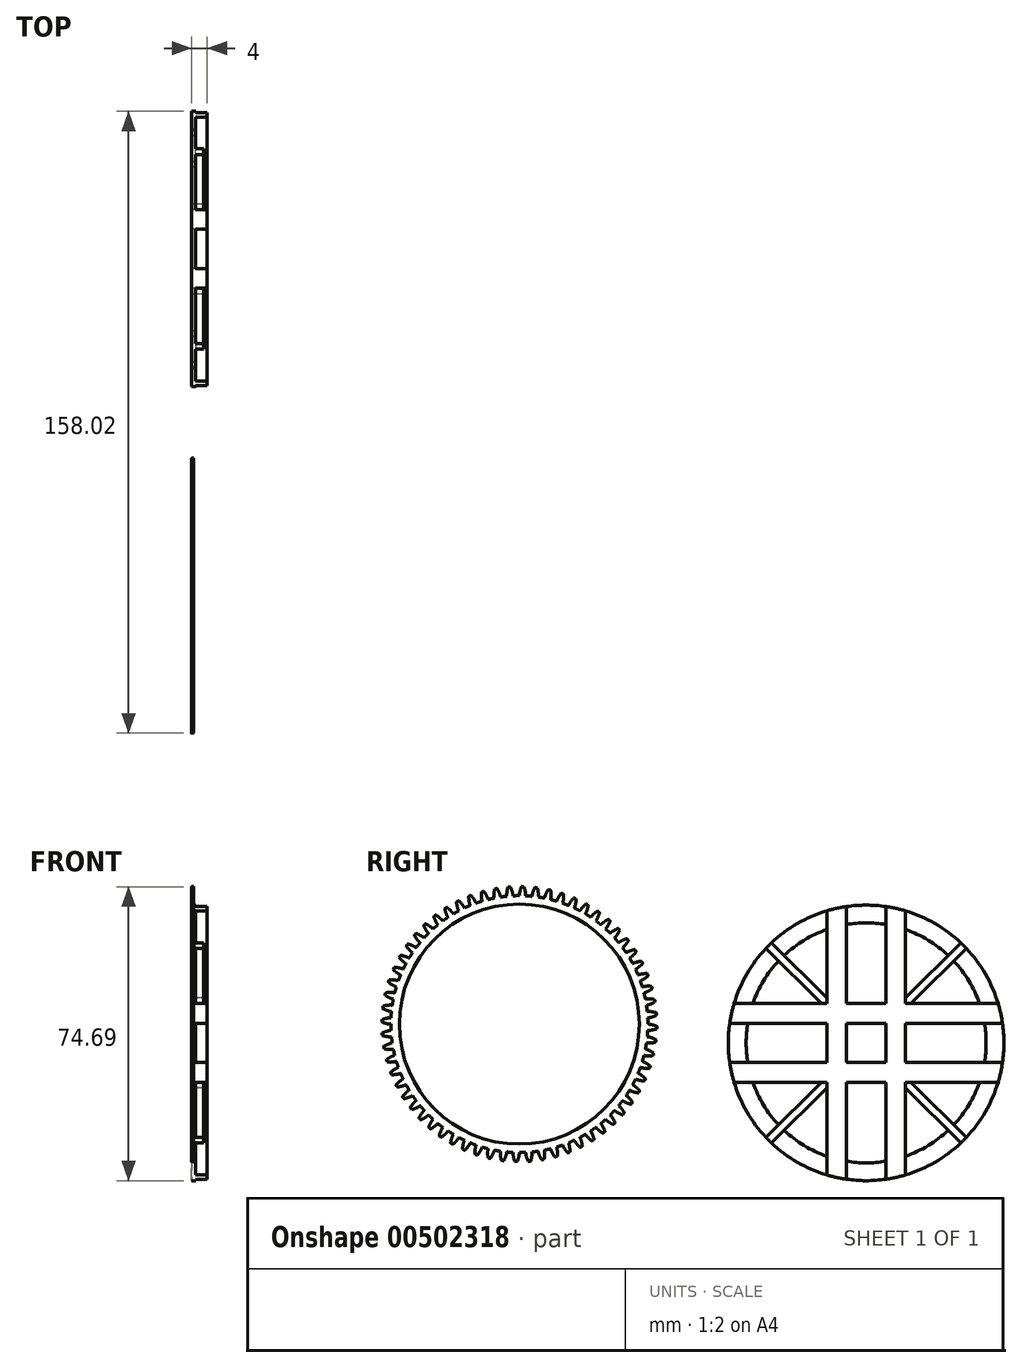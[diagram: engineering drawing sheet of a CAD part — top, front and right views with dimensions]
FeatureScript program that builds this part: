
annotation { "Feature Type Name" : "Feature", "Feature Type Description" : "" }
export const myFeature = defineFeature(function(context is Context, id is Id, definition is map)
    precondition{}
    {
        {
            assignVariable(context, id + "F0", {"name" : "NumberTeeth", "anyValue" : 64});
        }
        {
            assignVariable(context, id + "F1", {"name" : "GearThickness", "anyValue" : .5});
        }
        {
            var Q0;
            Q0=qCreatedBy(makeId("Right.planeOp"),FACE);
            var sketch = newSketch(context, id + "F2", { "sketchPlane" : qUnion([Q0])});
            skCircle(sketch, "E0", {"center": v(0, 0) * mm, "radius": 32.64 * mm});
            skCircle(sketch, "E1", {"center": v(0, 0) * mm, "radius": 32.79 * mm, "construction": true});
            skCircle(sketch, "E2", {"center": v(0, 0) * mm, "radius": 33.87 * mm, "construction": true});
            skCircle(sketch, "E3", {"center": v(0, 0) * mm, "radius": 34.93 * mm});
            skLineSegment(sketch, "E4", {"start": v(0, 0) * mm, "end": v(-32.79, 0) * mm, "construction": true});
            skLineSegment(sketch, "E5.1.0", {"start": v(0, 0) * mm, "end": v(-32.75, 1.64) * mm, "construction": true});
            skLineSegment(sketch, "E5.2.0", {"start": v(0, 0) * mm, "end": v(-32.62, 3.27) * mm, "construction": true});
            skLineSegment(sketch, "E5.3.0", {"start": v(0, 0) * mm, "end": v(-32.42, 4.9) * mm, "construction": true});
            skLineSegment(sketch, "E5.4.0", {"start": v(0, 0) * mm, "end": v(-32.13, 6.51) * mm, "construction": true});
            skLineSegment(sketch, "E5.5.0", {"start": v(0, 0) * mm, "end": v(-31.77, 8.11) * mm, "construction": true});
            skLineSegment(sketch, "E5.6.0", {"start": v(0, 0) * mm, "end": v(-31.32, 9.69) * mm, "construction": true});
            skLineSegment(sketch, "E5.7.0", {"start": v(0, 0) * mm, "end": v(-30.8, 11.24) * mm, "construction": true});
            skLineSegment(sketch, "E5.8.0", {"start": v(0, 0) * mm, "end": v(-30.2, 12.77) * mm, "construction": true});
            skLineSegment(sketch, "E5.9.0", {"start": v(0, 0) * mm, "end": v(-29.52, 14.26) * mm, "construction": true});
            skLineSegment(sketch, "E5.10.0", {"start": v(0, 0) * mm, "end": v(-28.77, 15.72) * mm, "construction": true});
            skLineSegment(sketch, "E5.11.0", {"start": v(0, 0) * mm, "end": v(-27.95, 17.14) * mm, "construction": true});
            skLineSegment(sketch, "E5.12.0", {"start": v(0, 0) * mm, "end": v(-27.06, 18.51) * mm, "construction": true});
            skLineSegment(sketch, "E5.13.0", {"start": v(0, 0) * mm, "end": v(-26.1, 19.84) * mm, "construction": true});
            skLineSegment(sketch, "E5.14.0", {"start": v(0, 0) * mm, "end": v(-25.08, 21.12) * mm, "construction": true});
            skLineSegment(sketch, "E5.anchor2", {"start": v(0, 0) * mm, "end": v(-25.08, 21.12) * mm, "construction": true});
            skLineSegment(sketch, "E6", {"start": v(-32.75, 1.64) * mm, "end": v(-32.83, 0) * mm, "construction": true});
            skLineSegment(sketch, "E7", {"start": v(-32.62, 3.27) * mm, "end": v(-32.95, 0.01) * mm, "construction": true});
            skLineSegment(sketch, "E8", {"start": v(-32.42, 4.9) * mm, "end": v(-33.15, 0.04) * mm, "construction": true});
            skLineSegment(sketch, "E9", {"start": v(-31.77, 8.11) * mm, "end": v(-33.8, 0.17) * mm, "construction": true});
            skLineSegment(sketch, "E10", {"start": v(-31.32, 9.69) * mm, "end": v(-34.23, 0.3) * mm, "construction": true});
            skLineSegment(sketch, "E11", {"start": v(-30.8, 11.24) * mm, "end": v(-34.74, 0.46) * mm, "construction": true});
            skLineSegment(sketch, "E12", {"start": v(-30.2, 12.77) * mm, "end": v(-35.3, 0.69) * mm, "construction": true});
            skLineSegment(sketch, "E13", {"start": v(-29.52, 14.26) * mm, "end": v(-35.94, 0.98) * mm, "construction": true});
            skLineSegment(sketch, "E14", {"start": v(-28.77, 15.72) * mm, "end": v(-36.63, 1.33) * mm, "construction": true});
            skLineSegment(sketch, "E15", {"start": v(-27.95, 17.14) * mm, "end": v(-37.38, 1.76) * mm, "construction": true});
            skLineSegment(sketch, "E16", {"start": v(-32.13, 6.51) * mm, "end": v(-33.44, 0.09) * mm, "construction": true});
            skLineSegment(sketch, "E17", {"start": v(-27.06, 18.51) * mm, "end": v(-38.17, 2.28) * mm, "construction": true});
            skLineSegment(sketch, "E18", {"start": v(-26.1, 19.84) * mm, "end": v(-39, 2.88) * mm, "construction": true});
            skLineSegment(sketch, "E19", {"start": v(-25.08, 21.12) * mm, "end": v(-39.86, 3.57) * mm, "construction": true});
            skLineSegment(sketch, "E20", {"start": v(0, 0) * mm, "end": v(-32.78, 0.8) * mm, "construction": true});
            skLineSegment(sketch, "E21", {"start": v(-32.64, 0) * mm, "end": v(-32.79, 0) * mm});
            skLineSegment(sketch, "E22.MirrorCS", {"start": v(-32.6, 1.6) * mm, "end": v(-32.75, 1.6) * mm});
            skFitSpline(sketch, "E23", {"points": [v(-32.79, 0) * mm, v(-32.83, 0) * mm, v(-32.95, 0.01) * mm, v(-33.15, 0.04) * mm, v(-33.44, 0.09) * mm, v(-33.8, 0.17) * mm, v(-34.23, 0.3) * mm, v(-34.74, 0.46) * mm, v(-35.3, 0.69) * mm, v(-35.94, 0.98) * mm, v(-36.63, 1.33) * mm, v(-37.38, 1.76) * mm, v(-38.17, 2.28) * mm, v(-39, 2.88) * mm, v(-39.86, 3.57) * mm], "startDerivative": vector(-0.7, 0) * mm, "endDerivative": vector(-1.66, 1.4) * mm});
            skLineSegment(sketch, "E24", {"start": v(-26.9, -7.36) * mm, "end": v(-39.86, 3.57) * mm, "construction": true});
            skFitSpline(sketch, "E25.MirrorCS", {"points": [v(-32.75, 1.6) * mm, v(-32.79, 1.6) * mm, v(-32.91, 1.6) * mm, v(-33.12, 1.6) * mm, v(-33.4, 1.55) * mm, v(-33.76, 1.49) * mm, v(-34.2, 1.39) * mm, v(-34.72, 1.24) * mm, v(-35.3, 1.04) * mm, v(-35.95, 0.79) * mm, v(-36.66, 0.47) * mm, v(-37.42, 0.07) * mm, v(-38.23, -0.4) * mm, v(-39.1, -0.96) * mm, v(-40, -1.6) * mm], "startDerivative": vector(-0.7, 0.03) * mm, "endDerivative": vector(-1.73, -1.32) * mm});
            skCircle(sketch, "E26", {"center": v(0, 0) * mm, "radius": 30.48 * mm});
            skSolve(sketch);
        }
        {
            var Q0;
            {var subQ0=sQuery(id+"F2.wireOp",EDGE,"E0");var subQ27=makeQuery(id+"F2.imprint","INTERSECT",VERTEX,{"derivedFrom":[subQ0,sQuery(id+"F2.wireOp",EDGE,"10ea1024-8cf5-41f5-a75f-a634b86921f3.10.0")]});Q0=makeQuery(id+"F2.imprint","IMPRINT",FACE,{"disambiguationData":[TD([[makeQuery(id+"F2.imprint","IMPRINT",EDGE,{"disambiguationData":[TD([[subQ27,-1.0]])],"derivedFrom":subQ0}),1.0]])]});}
            var Q1;
            {var subQ0=sQuery(id+"F2.wireOp",EDGE,"10ea1024-8cf5-41f5-a75f-a634b86921f3.1.0");Q1=makeQuery(id+"F2.imprint","IMPRINT",FACE,{"disambiguationData":[TD([[makeQuery(id+"F2.imprint","IMPRINT",EDGE,{"derivedFrom":subQ0}),-1.0]])]});}
            var Q2;
            {var subQ7=sQuery(id+"F2.wireOp",EDGE,"10ea1024-8cf5-41f5-a75f-a634b86921f3.2.0");Q2=makeQuery(id+"F2.imprint","IMPRINT",FACE,{"disambiguationData":[TD([[makeQuery(id+"F2.imprint","IMPRINT",EDGE,{"derivedFrom":subQ7}),-1.0]])]});}
            var Q3;
            {var subQ8=sQuery(id+"F2.wireOp",EDGE,"10ea1024-8cf5-41f5-a75f-a634b86921f3.3.0");Q3=makeQuery(id+"F2.imprint","IMPRINT",FACE,{"disambiguationData":[TD([[makeQuery(id+"F2.imprint","IMPRINT",EDGE,{"derivedFrom":subQ8}),-1.0]])]});}
            var Q4;
            {var subQ2=sQuery(id+"F2.wireOp",EDGE,"10ea1024-8cf5-41f5-a75f-a634b86921f3.4.0");Q4=makeQuery(id+"F2.imprint","IMPRINT",FACE,{"disambiguationData":[TD([[makeQuery(id+"F2.imprint","IMPRINT",EDGE,{"derivedFrom":subQ2}),-1.0]])]});}
            var Q5;
            {var subQ8=sQuery(id+"F2.wireOp",EDGE,"10ea1024-8cf5-41f5-a75f-a634b86921f3.5.0");Q5=makeQuery(id+"F2.imprint","IMPRINT",FACE,{"disambiguationData":[TD([[makeQuery(id+"F2.imprint","IMPRINT",EDGE,{"derivedFrom":subQ8}),-1.0]])]});}
            var Q6;
            {var subQ3=sQuery(id+"F2.wireOp",EDGE,"10ea1024-8cf5-41f5-a75f-a634b86921f3.6.0");Q6=makeQuery(id+"F2.imprint","IMPRINT",FACE,{"disambiguationData":[TD([[makeQuery(id+"F2.imprint","IMPRINT",EDGE,{"derivedFrom":subQ3}),-1.0]])]});}
            var Q7;
            {var subQ0=sQuery(id+"F2.wireOp",EDGE,"10ea1024-8cf5-41f5-a75f-a634b86921f3.7.0");Q7=makeQuery(id+"F2.imprint","IMPRINT",FACE,{"disambiguationData":[TD([[makeQuery(id+"F2.imprint","IMPRINT",EDGE,{"derivedFrom":subQ0}),-1.0]])]});}
            var Q8;
            {var subQ5=sQuery(id+"F2.wireOp",EDGE,"10ea1024-8cf5-41f5-a75f-a634b86921f3.8.0");Q8=makeQuery(id+"F2.imprint","IMPRINT",FACE,{"disambiguationData":[TD([[makeQuery(id+"F2.imprint","IMPRINT",EDGE,{"derivedFrom":subQ5}),-1.0]])]});}
            var Q9;
            {var subQ1=sQuery(id+"F2.wireOp",EDGE,"10ea1024-8cf5-41f5-a75f-a634b86921f3.9.0");Q9=makeQuery(id+"F2.imprint","IMPRINT",FACE,{"disambiguationData":[TD([[makeQuery(id+"F2.imprint","IMPRINT",EDGE,{"derivedFrom":subQ1}),-1.0]])]});}
            var Q10;
            {var subQ5=sQuery(id+"F2.wireOp",EDGE,"10ea1024-8cf5-41f5-a75f-a634b86921f3.10.0");Q10=makeQuery(id+"F2.imprint","IMPRINT",FACE,{"disambiguationData":[TD([[makeQuery(id+"F2.imprint","IMPRINT",EDGE,{"derivedFrom":subQ5}),-1.0]])]});}
            var Q11;
            {var subQ8=sQuery(id+"F2.wireOp",EDGE,"10ea1024-8cf5-41f5-a75f-a634b86921f3.11.0");Q11=makeQuery(id+"F2.imprint","IMPRINT",FACE,{"disambiguationData":[TD([[makeQuery(id+"F2.imprint","IMPRINT",EDGE,{"derivedFrom":subQ8}),-1.0]])]});}
            var Q12;
            {var subQ2=sQuery(id+"F2.wireOp",EDGE,"10ea1024-8cf5-41f5-a75f-a634b86921f3.12.0");Q12=makeQuery(id+"F2.imprint","IMPRINT",FACE,{"disambiguationData":[TD([[makeQuery(id+"F2.imprint","IMPRINT",EDGE,{"derivedFrom":subQ2}),-1.0]])]});}
            var Q13;
            {var subQ3=sQuery(id+"F2.wireOp",EDGE,"10ea1024-8cf5-41f5-a75f-a634b86921f3.13.0");Q13=makeQuery(id+"F2.imprint","IMPRINT",FACE,{"disambiguationData":[TD([[makeQuery(id+"F2.imprint","IMPRINT",EDGE,{"derivedFrom":subQ3}),-1.0]])]});}
            var Q14;
            {var subQ0=sQuery(id+"F2.wireOp",EDGE,"10ea1024-8cf5-41f5-a75f-a634b86921f3.14.0");Q14=makeQuery(id+"F2.imprint","IMPRINT",FACE,{"disambiguationData":[TD([[makeQuery(id+"F2.imprint","IMPRINT",EDGE,{"derivedFrom":subQ0}),-1.0]])]});}
            var Q15;
            {var subQ6=sQuery(id+"F2.wireOp",EDGE,"10ea1024-8cf5-41f5-a75f-a634b86921f3.15.0");Q15=makeQuery(id+"F2.imprint","IMPRINT",FACE,{"disambiguationData":[TD([[makeQuery(id+"F2.imprint","IMPRINT",EDGE,{"derivedFrom":subQ6}),-1.0]])]});}
            var Q16;
            {var subQ5=sQuery(id+"F2.wireOp",EDGE,"10ea1024-8cf5-41f5-a75f-a634b86921f3.16.0");Q16=makeQuery(id+"F2.imprint","IMPRINT",FACE,{"disambiguationData":[TD([[makeQuery(id+"F2.imprint","IMPRINT",EDGE,{"derivedFrom":subQ5}),-1.0]])]});}
            var Q17;
            {var subQ7=sQuery(id+"F2.wireOp",EDGE,"10ea1024-8cf5-41f5-a75f-a634b86921f3.17.0");Q17=makeQuery(id+"F2.imprint","IMPRINT",FACE,{"disambiguationData":[TD([[makeQuery(id+"F2.imprint","IMPRINT",EDGE,{"derivedFrom":subQ7}),-1.0]])]});}
            var Q18;
            {var subQ5=sQuery(id+"F2.wireOp",EDGE,"10ea1024-8cf5-41f5-a75f-a634b86921f3.18.0");Q18=makeQuery(id+"F2.imprint","IMPRINT",FACE,{"disambiguationData":[TD([[makeQuery(id+"F2.imprint","IMPRINT",EDGE,{"derivedFrom":subQ5}),-1.0]])]});}
            var Q19;
            {var subQ8=sQuery(id+"F2.wireOp",EDGE,"10ea1024-8cf5-41f5-a75f-a634b86921f3.19.0");Q19=makeQuery(id+"F2.imprint","IMPRINT",FACE,{"disambiguationData":[TD([[makeQuery(id+"F2.imprint","IMPRINT",EDGE,{"derivedFrom":subQ8}),-1.0]])]});}
            var Q20;
            {var subQ8=sQuery(id+"F2.wireOp",EDGE,"E21");Q20=makeQuery(id+"F2.imprint","IMPRINT",FACE,{"disambiguationData":[TD([[makeQuery(id+"F2.imprint","IMPRINT",EDGE,{"derivedFrom":subQ8}),-1.0]])]});}
            extrude(context, id + "F3", {"entities" : qUnion([Q0, Q1, Q2, Q3, Q4, Q5, Q6, Q7, Q8, Q9, Q10, Q11, Q12, Q13, Q14, Q15, Q16, Q17, Q18, Q19, Q20]), "depth" : (getVariable(context, 'GearThickness')) * mm});
        }
        {
            var Q0;
            Q0=makeQuery(id+"F3.opExtrude","SWEPT_FACE",FACE,{"disambiguationData":[OSD([sQuery(id+"F2.wireOp",EDGE,"E25.MirrorCS")])]});
            var Q1;
            Q1=makeQuery(id+"F3.opExtrude","SWEPT_FACE",FACE,{"disambiguationData":[OSD([sQuery(id+"F2.wireOp",EDGE,"E23")])]});
            var Q2;
            Q2=makeQuery(id+"F3.opExtrude","SWEPT_FACE",FACE,{"disambiguationData":[OSD([sQuery(id+"F2.wireOp",EDGE,"E3")])]});
            var Q3;
            Q3=makeQuery(id+"F3.opExtrude","SWEPT_FACE",FACE,{"disambiguationData":[OSD([sQuery(id+"F2.wireOp",EDGE,"E22.MirrorCS")])]});
            var Q4;
            Q4=makeQuery(id+"F3.opExtrude","SWEPT_FACE",FACE,{"disambiguationData":[OSD([sQuery(id+"F2.wireOp",EDGE,"E21")])]});
            var Q5;
            Q5=makeQuery(id+"F3.opExtrude","SWEPT_FACE",FACE,{"disambiguationData":[OSD([sQuery(id+"F2.wireOp",EDGE,"E0")])]});
            circularPattern(context, id + "F4", {"faces" : qUnion([Q0, Q1, Q2, Q3, Q4]), "axis" : qUnion([Q5]), "angle" : 360 * degree, "instanceCount" : getVariable(context, 'NumberTeeth'), "equalSpace" : true, "patternType" : PatternType.FACE});
        }
        {
            var Q0;
            Q0=qCreatedBy(makeId("Right.planeOp"),FACE);
            var sketch = newSketch(context, id + "F5", { "sketchPlane" : qUnion([Q0])});
            skCircle(sketch, "E27", {"center": v(88.1, -4.77) * mm, "radius": 35 * mm});
            skLineSegment(sketch, "E28", {"start": v(93.1, -9.77) * mm, "end": v(93.1, 0.23) * mm});
            skLineSegment(sketch, "E29.0", {"start": v(98.1, -9.77) * mm, "end": v(98.1, 0.23) * mm});
            skLineSegment(sketch, "E30", {"start": v(88.1, 30.23) * mm, "end": v(88.1, -39.77) * mm, "construction": true});
            skLineSegment(sketch, "E31", {"start": v(53.1, -4.77) * mm, "end": v(123.1, -4.77) * mm, "construction": true});
            skLineSegment(sketch, "E32.MirrorCS", {"start": v(78.1, -9.77) * mm, "end": v(78.1, 0.23) * mm});
            skLineSegment(sketch, "E33.MirrorCS", {"start": v(83.1, -9.77) * mm, "end": v(83.1, 0.23) * mm});
            skLineSegment(sketch, "E34.MirrorCS", {"start": v(98.1, 0.23) * mm, "end": v(98.1, -9.77) * mm});
            skLineSegment(sketch, "E35.MirrorCS", {"start": v(93.1, 0.23) * mm, "end": v(93.1, -9.77) * mm});
            skLineSegment(sketch, "E36.MirrorCS", {"start": v(78.1, 0.23) * mm, "end": v(78.1, -9.77) * mm});
            skLineSegment(sketch, "E37.MirrorCS", {"start": v(83.1, 0.23) * mm, "end": v(83.1, -9.77) * mm});
            skLineSegment(sketch, "E38.0", {"start": v(53.46, -9.77) * mm, "end": v(78.1, -9.77) * mm});
            skLineSegment(sketch, "E39.0", {"start": v(54.56, -14.77) * mm, "end": v(78.1, -14.77) * mm});
            skLineSegment(sketch, "E40.MirrorCS", {"start": v(53.46, 0.23) * mm, "end": v(78.1, 0.23) * mm});
            skLineSegment(sketch, "E41.MirrorCS", {"start": v(54.56, 5.23) * mm, "end": v(78.1, 5.23) * mm});
            skLineSegment(sketch, "E42.trimOffspring", {"start": v(78.1, 5.23) * mm, "end": v(78.1, 28.77) * mm});
            skLineSegment(sketch, "E43.trimOffspring", {"start": v(83.1, 5.23) * mm, "end": v(93.1, 5.23) * mm});
            skLineSegment(sketch, "E44.trimOffspring", {"start": v(83.1, 5.23) * mm, "end": v(83.1, 29.87) * mm});
            skLineSegment(sketch, "E45.trimOffspring", {"start": v(83.1, 0.23) * mm, "end": v(93.1, 0.23) * mm});
            skLineSegment(sketch, "E46.trimOffspring", {"start": v(83.1, -9.77) * mm, "end": v(93.1, -9.77) * mm});
            skLineSegment(sketch, "E47.trimOffspring", {"start": v(78.1, -14.77) * mm, "end": v(78.1, -38.3) * mm});
            skLineSegment(sketch, "E48.trimOffspring", {"start": v(83.1, -14.77) * mm, "end": v(83.1, -39.4) * mm});
            skLineSegment(sketch, "E49.trimOffspring", {"start": v(83.1, -14.77) * mm, "end": v(93.1, -14.77) * mm});
            skLineSegment(sketch, "E50.trimOffspring", {"start": v(93.1, -14.77) * mm, "end": v(93.1, -39.4) * mm});
            skLineSegment(sketch, "E51.trimOffspring", {"start": v(98.1, -14.77) * mm, "end": v(121.64, -14.77) * mm});
            skLineSegment(sketch, "E52.trimOffspring", {"start": v(98.1, -9.77) * mm, "end": v(122.74, -9.77) * mm});
            skLineSegment(sketch, "E53.trimOffspring", {"start": v(98.1, -14.77) * mm, "end": v(98.1, -38.3) * mm});
            skLineSegment(sketch, "E54.trimOffspring", {"start": v(98.1, 0.23) * mm, "end": v(122.74, 0.23) * mm});
            skLineSegment(sketch, "E55.trimOffspring", {"start": v(98.1, 5.23) * mm, "end": v(98.1, 28.77) * mm});
            skLineSegment(sketch, "E56.trimOffspring", {"start": v(98.1, 5.23) * mm, "end": v(121.64, 5.23) * mm});
            skLineSegment(sketch, "E57.trimOffspring", {"start": v(93.1, 5.23) * mm, "end": v(93.1, 29.87) * mm});
            skLineSegment(sketch, "E58", {"start": v(88.1, -4.77) * mm, "end": v(112.85, 19.98) * mm, "construction": true});
            skLineSegment(sketch, "E59", {"start": v(78.1, 5.23) * mm, "end": v(98.1, -14.77) * mm, "construction": true});
            skCircle(sketch, "E60", {"center": v(88.1, -4.77) * mm, "radius": 30.48 * mm});
            skLineSegment(sketch, "E61.0", {"start": v(99.52, 5.23) * mm, "end": v(113.56, 19.27) * mm});
            skLineSegment(sketch, "E62.0", {"start": v(98.1, 6.65) * mm, "end": v(112.14, 20.69) * mm});
            skLineSegment(sketch, "E63.MirrorCS", {"start": v(78.1, 6.65) * mm, "end": v(64.06, 20.69) * mm});
            skLineSegment(sketch, "E64.MirrorCS", {"start": v(76.69, 5.23) * mm, "end": v(62.65, 19.27) * mm});
            skLineSegment(sketch, "E65.MirrorCS", {"start": v(99.52, -14.77) * mm, "end": v(113.56, -28.81) * mm});
            skLineSegment(sketch, "E66.MirrorCS", {"start": v(98.1, -16.18) * mm, "end": v(112.14, -30.22) * mm});
            skLineSegment(sketch, "E67.MirrorCS", {"start": v(78.1, -16.18) * mm, "end": v(64.06, -30.22) * mm});
            skLineSegment(sketch, "E68.MirrorCS", {"start": v(76.69, -14.77) * mm, "end": v(62.65, -28.81) * mm});
            skSolve(sketch);
        }
        {
            var Q0;
            Q0=makeQuery(id+"F5.imprint","IMPRINT",FACE,{"disambiguationData":[TD([[makeQuery(id+"F5.imprint","IMPRINT",EDGE,{"derivedFrom":sQuery(id+"F5.wireOp",EDGE,"E28")}),-1.0]])]});
            var Q1;
            {var subQ0=sQuery(id+"F5.wireOp",EDGE,"E42.trimOffspring");var subQ1=sQuery(id+"F5.wireOp",EDGE,"E27");var subQ2=makeQuery(id+"F5.imprint","INTERSECT",VERTEX,{"derivedFrom":[subQ1,subQ0]});Q1=makeQuery(id+"F5.imprint","IMPRINT",FACE,{"disambiguationData":[TD([[makeQuery(id+"F5.imprint","IMPRINT",EDGE,{"disambiguationData":[TD([[subQ2,1.0]])],"derivedFrom":subQ1}),1.0]])]});}
            var Q2;
            {var subQ0=sQuery(id+"F5.wireOp",EDGE,"E55.trimOffspring");var subQ1=sQuery(id+"F5.wireOp",EDGE,"E27");var subQ2=makeQuery(id+"F5.imprint","INTERSECT",VERTEX,{"derivedFrom":[subQ1,subQ0]});Q2=makeQuery(id+"F5.imprint","IMPRINT",FACE,{"disambiguationData":[TD([[makeQuery(id+"F5.imprint","IMPRINT",EDGE,{"disambiguationData":[TD([[subQ2,-1.0]])],"derivedFrom":subQ1}),1.0]])]});}
            var Q3;
            {var subQ0=sQuery(id+"F5.wireOp",EDGE,"E54.trimOffspring");var subQ1=sQuery(id+"F5.wireOp",EDGE,"E27");var subQ2=makeQuery(id+"F5.imprint","INTERSECT",VERTEX,{"derivedFrom":[subQ1,subQ0]});Q3=makeQuery(id+"F5.imprint","IMPRINT",FACE,{"disambiguationData":[TD([[makeQuery(id+"F5.imprint","IMPRINT",EDGE,{"disambiguationData":[TD([[subQ2,-1.0]])],"derivedFrom":subQ1}),1.0]])]});}
            var Q4;
            {var subQ0=sQuery(id+"F5.wireOp",EDGE,"E51.trimOffspring");var subQ1=sQuery(id+"F5.wireOp",EDGE,"E27");var subQ2=makeQuery(id+"F5.imprint","INTERSECT",VERTEX,{"derivedFrom":[subQ1,subQ0]});Q4=makeQuery(id+"F5.imprint","IMPRINT",FACE,{"disambiguationData":[TD([[makeQuery(id+"F5.imprint","IMPRINT",EDGE,{"disambiguationData":[TD([[subQ2,-1.0]])],"derivedFrom":subQ1}),1.0]])]});}
            var Q5;
            {var subQ0=sQuery(id+"F5.wireOp",EDGE,"E50.trimOffspring");var subQ1=sQuery(id+"F5.wireOp",EDGE,"E27");var subQ2=makeQuery(id+"F5.imprint","INTERSECT",VERTEX,{"derivedFrom":[subQ1,subQ0]});Q5=makeQuery(id+"F5.imprint","IMPRINT",FACE,{"disambiguationData":[TD([[makeQuery(id+"F5.imprint","IMPRINT",EDGE,{"disambiguationData":[TD([[subQ2,-1.0]])],"derivedFrom":subQ1}),1.0]])]});}
            var Q6;
            {var subQ0=sQuery(id+"F5.wireOp",EDGE,"E47.trimOffspring");var subQ1=sQuery(id+"F5.wireOp",EDGE,"E27");var subQ2=makeQuery(id+"F5.imprint","INTERSECT",VERTEX,{"derivedFrom":[subQ1,subQ0]});Q6=makeQuery(id+"F5.imprint","IMPRINT",FACE,{"disambiguationData":[TD([[makeQuery(id+"F5.imprint","IMPRINT",EDGE,{"disambiguationData":[TD([[subQ2,-1.0]])],"derivedFrom":subQ1}),1.0]])]});}
            var Q7;
            {var subQ0=sQuery(id+"F5.wireOp",EDGE,"E38.0");var subQ1=sQuery(id+"F5.wireOp",EDGE,"E27");var subQ2=makeQuery(id+"F5.imprint","INTERSECT",VERTEX,{"derivedFrom":[subQ1,subQ0]});Q7=makeQuery(id+"F5.imprint","IMPRINT",FACE,{"disambiguationData":[TD([[makeQuery(id+"F5.imprint","IMPRINT",EDGE,{"disambiguationData":[TD([[subQ2,-1.0]])],"derivedFrom":subQ1}),1.0]])]});}
            var Q8;
            {var subQ0=sQuery(id+"F5.wireOp",EDGE,"E40.MirrorCS");var subQ1=sQuery(id+"F5.wireOp",EDGE,"E27");var subQ2=makeQuery(id+"F5.imprint","INTERSECT",VERTEX,{"derivedFrom":[subQ1,subQ0]});Q8=makeQuery(id+"F5.imprint","IMPRINT",FACE,{"disambiguationData":[TD([[makeQuery(id+"F5.imprint","IMPRINT",EDGE,{"disambiguationData":[TD([[subQ2,1.0]])],"derivedFrom":subQ1}),1.0]])]});}
            var Q9;
            {var subQ31=sQuery(id+"F5.wireOp",EDGE,"E34.MirrorCS");Q9=makeQuery(id+"F5.imprint","IMPRINT",FACE,{"disambiguationData":[TD([[makeQuery(id+"F5.imprint","IMPRINT",EDGE,{"derivedFrom":subQ31}),-1.0]])]});}
            extrude(context, id + "F6", {"entities" : qUnion([Q0, Q1, Q2, Q3, Q4, Q5, Q6, Q7, Q8, Q9]), "depth" : 4 * mm});
        }
        {
            var Q0;
            {var subQ0=sQuery(id+"F5.wireOp",EDGE,"E42.trimOffspring");var subQ1=sQuery(id+"F5.wireOp",EDGE,"E27");var subQ2=makeQuery(id+"F5.imprint","INTERSECT",VERTEX,{"derivedFrom":[subQ1,subQ0]});Q0=makeQuery(id+"F5.imprint","IMPRINT",FACE,{"disambiguationData":[TD([[makeQuery(id+"F5.imprint","IMPRINT",EDGE,{"disambiguationData":[TD([[subQ2,-1.0]])],"derivedFrom":subQ1}),1.0]])]});}
            var Q1;
            {var subQ0=sQuery(id+"F5.wireOp",EDGE,"E44.trimOffspring");var subQ1=sQuery(id+"F5.wireOp",EDGE,"E27");var subQ2=makeQuery(id+"F5.imprint","INTERSECT",VERTEX,{"derivedFrom":[subQ1,subQ0]});Q1=makeQuery(id+"F5.imprint","IMPRINT",FACE,{"disambiguationData":[TD([[makeQuery(id+"F5.imprint","IMPRINT",EDGE,{"disambiguationData":[TD([[subQ2,1.0]])],"derivedFrom":subQ1}),1.0]])]});}
            var Q2;
            {var subQ0=sQuery(id+"F5.wireOp",EDGE,"E55.trimOffspring");var subQ1=sQuery(id+"F5.wireOp",EDGE,"E27");var subQ2=makeQuery(id+"F5.imprint","INTERSECT",VERTEX,{"derivedFrom":[subQ1,subQ0]});Q2=makeQuery(id+"F5.imprint","IMPRINT",FACE,{"disambiguationData":[TD([[makeQuery(id+"F5.imprint","IMPRINT",EDGE,{"disambiguationData":[TD([[subQ2,1.0]])],"derivedFrom":subQ1}),1.0]])]});}
            var Q3;
            {var subQ0=sQuery(id+"F5.wireOp",EDGE,"E56.trimOffspring");var subQ1=sQuery(id+"F5.wireOp",EDGE,"E27");var subQ2=makeQuery(id+"F5.imprint","INTERSECT",VERTEX,{"derivedFrom":[subQ1,subQ0]});Q3=makeQuery(id+"F5.imprint","IMPRINT",FACE,{"disambiguationData":[TD([[makeQuery(id+"F5.imprint","IMPRINT",EDGE,{"disambiguationData":[TD([[subQ2,-1.0]])],"derivedFrom":subQ1}),1.0]])]});}
            var Q4;
            {var subQ0=sQuery(id+"F5.wireOp",EDGE,"E52.trimOffspring");var subQ1=sQuery(id+"F5.wireOp",EDGE,"E27");var subQ2=makeQuery(id+"F5.imprint","INTERSECT",VERTEX,{"derivedFrom":[subQ1,subQ0]});Q4=makeQuery(id+"F5.imprint","IMPRINT",FACE,{"disambiguationData":[TD([[makeQuery(id+"F5.imprint","IMPRINT",EDGE,{"disambiguationData":[TD([[subQ2,-1.0]])],"derivedFrom":subQ1}),1.0]])]});}
            var Q5;
            {var subQ0=sQuery(id+"F5.wireOp",EDGE,"E51.trimOffspring");var subQ1=sQuery(id+"F5.wireOp",EDGE,"E27");var subQ2=makeQuery(id+"F5.imprint","INTERSECT",VERTEX,{"derivedFrom":[subQ1,subQ0]});Q5=makeQuery(id+"F5.imprint","IMPRINT",FACE,{"disambiguationData":[TD([[makeQuery(id+"F5.imprint","IMPRINT",EDGE,{"disambiguationData":[TD([[subQ2,1.0]])],"derivedFrom":subQ1}),1.0]])]});}
            var Q6;
            {var subQ0=sQuery(id+"F5.wireOp",EDGE,"E53.trimOffspring");var subQ1=sQuery(id+"F5.wireOp",EDGE,"E27");var subQ2=makeQuery(id+"F5.imprint","INTERSECT",VERTEX,{"derivedFrom":[subQ1,subQ0]});Q6=makeQuery(id+"F5.imprint","IMPRINT",FACE,{"disambiguationData":[TD([[makeQuery(id+"F5.imprint","IMPRINT",EDGE,{"disambiguationData":[TD([[subQ2,-1.0]])],"derivedFrom":subQ1}),1.0]])]});}
            var Q7;
            {var subQ0=sQuery(id+"F5.wireOp",EDGE,"E48.trimOffspring");var subQ1=sQuery(id+"F5.wireOp",EDGE,"E27");var subQ2=makeQuery(id+"F5.imprint","INTERSECT",VERTEX,{"derivedFrom":[subQ1,subQ0]});Q7=makeQuery(id+"F5.imprint","IMPRINT",FACE,{"disambiguationData":[TD([[makeQuery(id+"F5.imprint","IMPRINT",EDGE,{"disambiguationData":[TD([[subQ2,-1.0]])],"derivedFrom":subQ1}),1.0]])]});}
            var Q8;
            {var subQ0=sQuery(id+"F5.wireOp",EDGE,"E47.trimOffspring");var subQ1=sQuery(id+"F5.wireOp",EDGE,"E27");var subQ2=makeQuery(id+"F5.imprint","INTERSECT",VERTEX,{"derivedFrom":[subQ1,subQ0]});Q8=makeQuery(id+"F5.imprint","IMPRINT",FACE,{"disambiguationData":[TD([[makeQuery(id+"F5.imprint","IMPRINT",EDGE,{"disambiguationData":[TD([[subQ2,1.0]])],"derivedFrom":subQ1}),1.0]])]});}
            var Q9;
            {var subQ0=sQuery(id+"F5.wireOp",EDGE,"E39.0");var subQ1=sQuery(id+"F5.wireOp",EDGE,"E27");var subQ2=makeQuery(id+"F5.imprint","INTERSECT",VERTEX,{"derivedFrom":[subQ1,subQ0]});Q9=makeQuery(id+"F5.imprint","IMPRINT",FACE,{"disambiguationData":[TD([[makeQuery(id+"F5.imprint","IMPRINT",EDGE,{"disambiguationData":[TD([[subQ2,-1.0]])],"derivedFrom":subQ1}),1.0]])]});}
            var Q10;
            {var subQ0=sQuery(id+"F5.wireOp",EDGE,"E38.0");var subQ1=sQuery(id+"F5.wireOp",EDGE,"E27");var subQ2=makeQuery(id+"F5.imprint","INTERSECT",VERTEX,{"derivedFrom":[subQ1,subQ0]});Q10=makeQuery(id+"F5.imprint","IMPRINT",FACE,{"disambiguationData":[TD([[makeQuery(id+"F5.imprint","IMPRINT",EDGE,{"disambiguationData":[TD([[subQ2,1.0]])],"derivedFrom":subQ1}),1.0]])]});}
            var Q11;
            {var subQ0=sQuery(id+"F5.wireOp",EDGE,"E41.MirrorCS");var subQ1=sQuery(id+"F5.wireOp",EDGE,"E27");var subQ2=makeQuery(id+"F5.imprint","INTERSECT",VERTEX,{"derivedFrom":[subQ1,subQ0]});Q11=makeQuery(id+"F5.imprint","IMPRINT",FACE,{"disambiguationData":[TD([[makeQuery(id+"F5.imprint","IMPRINT",EDGE,{"disambiguationData":[TD([[subQ2,1.0]])],"derivedFrom":subQ1}),1.0]])]});}
            extrude(context, id + "F7", {"entities" : qUnion([Q0, Q1, Q2, Q3, Q4, Q5, Q6, Q7, Q8, Q9, Q10, Q11]), "operationType" : NewBodyOperationType.ADD, "depth" : 1 * mm});
        }
        {
            var Q0;
            {var subQ0=sQuery(id+"F5.wireOp",EDGE,"E63.MirrorCS");var subQ1=sQuery(id+"F5.wireOp",EDGE,"E27");var subQ2=makeQuery(id+"F5.imprint","INTERSECT",VERTEX,{"derivedFrom":[subQ1,subQ0]});Q0=makeQuery(id+"F5.imprint","IMPRINT",FACE,{"disambiguationData":[TD([[makeQuery(id+"F5.imprint","IMPRINT",EDGE,{"disambiguationData":[TD([[subQ2,-1.0]])],"derivedFrom":subQ1}),1.0]])]});}
            var Q1;
            {var subQ1=sQuery(id+"F5.wireOp",EDGE,"E42.trimOffspring");var subQ7=sQuery(id+"F5.wireOp",EDGE,"E41.MirrorCS");var subQ9=makeQuery(id+"F5.imprint","INTERSECT",VERTEX,{"derivedFrom":[subQ7,subQ1]});Q1=makeQuery(id+"F5.imprint","IMPRINT",FACE,{"disambiguationData":[TD([[makeQuery(id+"F5.imprint","IMPRINT",EDGE,{"disambiguationData":[TD([[subQ9,1.0]])],"derivedFrom":subQ7}),1.0]])]});}
            var Q2;
            {var subQ0=sQuery(id+"F5.wireOp",EDGE,"E68.MirrorCS");var subQ1=sQuery(id+"F5.wireOp",EDGE,"E27");var subQ2=makeQuery(id+"F5.imprint","INTERSECT",VERTEX,{"derivedFrom":[subQ1,subQ0]});Q2=makeQuery(id+"F5.imprint","IMPRINT",FACE,{"disambiguationData":[TD([[makeQuery(id+"F5.imprint","IMPRINT",EDGE,{"disambiguationData":[TD([[subQ2,-1.0]])],"derivedFrom":subQ1}),1.0]])]});}
            var Q3;
            {var subQ1=sQuery(id+"F5.wireOp",EDGE,"E47.trimOffspring");var subQ7=sQuery(id+"F5.wireOp",EDGE,"E39.0");var subQ8=makeQuery(id+"F5.imprint","INTERSECT",VERTEX,{"derivedFrom":[subQ7,subQ1]});Q3=makeQuery(id+"F5.imprint","IMPRINT",FACE,{"disambiguationData":[TD([[makeQuery(id+"F5.imprint","IMPRINT",EDGE,{"disambiguationData":[TD([[subQ8,1.0]])],"derivedFrom":subQ7}),-1.0]])]});}
            var Q4;
            {var subQ0=sQuery(id+"F5.wireOp",EDGE,"E66.MirrorCS");var subQ1=sQuery(id+"F5.wireOp",EDGE,"E27");var subQ2=makeQuery(id+"F5.imprint","INTERSECT",VERTEX,{"derivedFrom":[subQ1,subQ0]});Q4=makeQuery(id+"F5.imprint","IMPRINT",FACE,{"disambiguationData":[TD([[makeQuery(id+"F5.imprint","IMPRINT",EDGE,{"disambiguationData":[TD([[subQ2,-1.0]])],"derivedFrom":subQ1}),1.0]])]});}
            var Q5;
            {var subQ5=sQuery(id+"F5.wireOp",EDGE,"E53.trimOffspring");var subQ6=sQuery(id+"F5.wireOp",EDGE,"E51.trimOffspring");var subQ7=makeQuery(id+"F5.imprint","INTERSECT",VERTEX,{"derivedFrom":[subQ6,subQ5]});Q5=makeQuery(id+"F5.imprint","IMPRINT",FACE,{"disambiguationData":[TD([[makeQuery(id+"F5.imprint","IMPRINT",EDGE,{"disambiguationData":[TD([[subQ7,-1.0]])],"derivedFrom":subQ6}),-1.0]])]});}
            var Q6;
            {var subQ1=sQuery(id+"F5.wireOp",EDGE,"E56.trimOffspring");var subQ7=sQuery(id+"F5.wireOp",EDGE,"E55.trimOffspring");var subQ8=makeQuery(id+"F5.imprint","INTERSECT",VERTEX,{"derivedFrom":[subQ7,subQ1]});Q6=makeQuery(id+"F5.imprint","IMPRINT",FACE,{"disambiguationData":[TD([[makeQuery(id+"F5.imprint","IMPRINT",EDGE,{"disambiguationData":[TD([[subQ8,-1.0]])],"derivedFrom":subQ7}),-1.0]])]});}
            var Q7;
            {var subQ0=sQuery(id+"F5.wireOp",EDGE,"E61.0");var subQ1=sQuery(id+"F5.wireOp",EDGE,"E27");var subQ2=makeQuery(id+"F5.imprint","INTERSECT",VERTEX,{"derivedFrom":[subQ1,subQ0]});Q7=makeQuery(id+"F5.imprint","IMPRINT",FACE,{"disambiguationData":[TD([[makeQuery(id+"F5.imprint","IMPRINT",EDGE,{"disambiguationData":[TD([[subQ2,-1.0]])],"derivedFrom":subQ1}),1.0]])]});}
            extrude(context, id + "F8", {"entities" : qUnion([Q0, Q1, Q2, Q3, Q4, Q5, Q6, Q7]), "operationType" : NewBodyOperationType.ADD, "depth" : 3 * mm});
        }
    });
